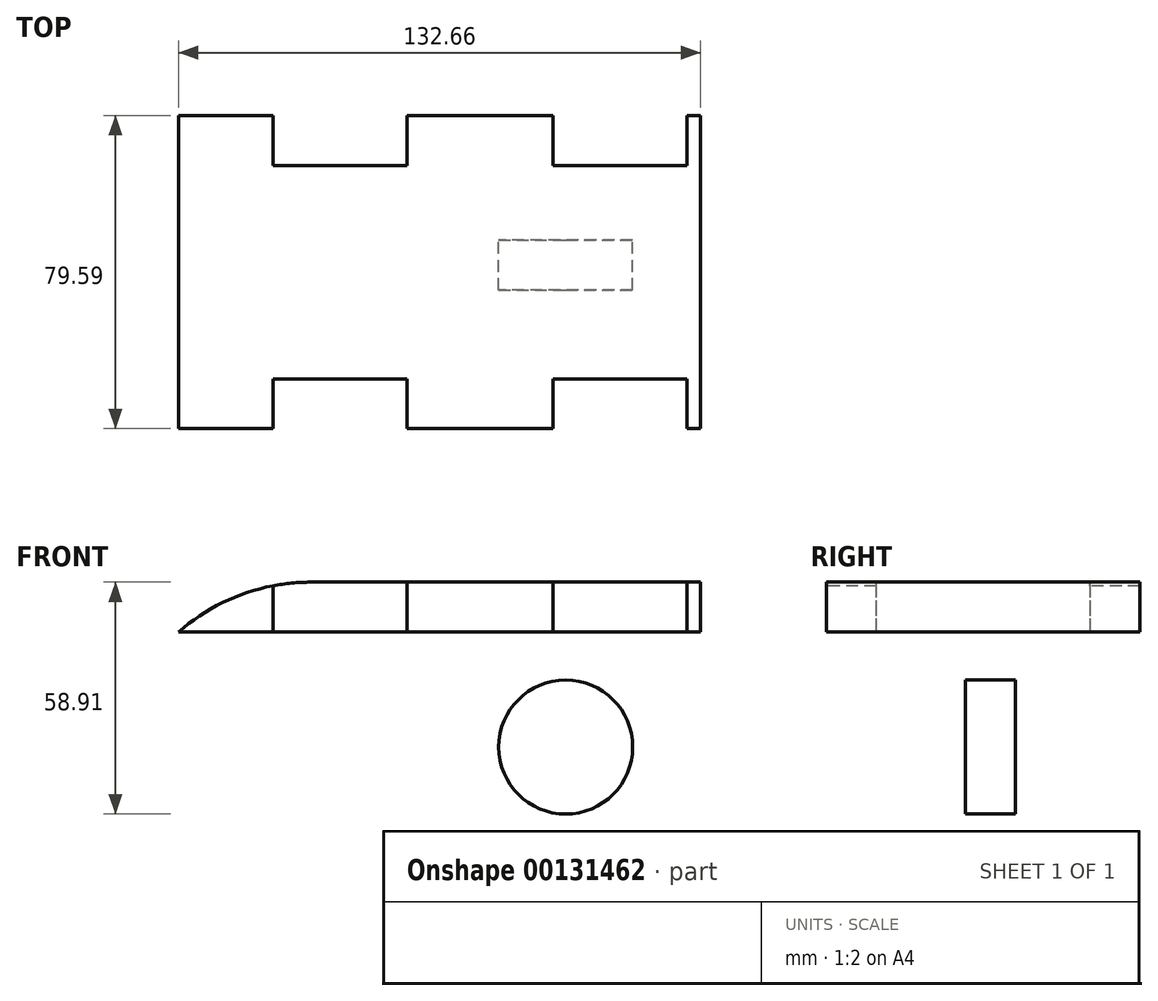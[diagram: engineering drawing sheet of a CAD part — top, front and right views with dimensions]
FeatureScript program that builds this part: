
annotation { "Feature Type Name" : "Feature", "Feature Type Description" : "" }
export const myFeature = defineFeature(function(context is Context, id is Id, definition is map)
    precondition{}
    {
        {
            var Q0;
            Q0=qCreatedBy(makeId("Top.planeOp"),FACE);
            var sketch = newSketch(context, id + "F0", { "sketchPlane" : qUnion([Q0])});
            skLineSegment(sketch, "E0.bottom", {"start": v(-58.03, 31.64) * mm, "end": v(74.63, 31.64) * mm});
            skLineSegment(sketch, "E0.top", {"start": v(-58.03, -47.95) * mm, "end": v(74.63, -47.95) * mm});
            skLineSegment(sketch, "E0.left", {"start": v(-58.03, 31.64) * mm, "end": v(-58.03, -47.95) * mm});
            skLineSegment(sketch, "E0.right", {"start": v(74.63, 31.64) * mm, "end": v(74.63, -47.95) * mm});
            skLineSegment(sketch, "E1.bottom", {"start": v(-34.04, 31.64) * mm, "end": v(0, 31.64) * mm});
            skLineSegment(sketch, "E1.top", {"start": v(-34.04, 18.94) * mm, "end": v(0, 18.94) * mm});
            skLineSegment(sketch, "E1.left", {"start": v(-34.04, 31.64) * mm, "end": v(-34.04, 18.94) * mm});
            skLineSegment(sketch, "E1.right", {"start": v(0, 31.64) * mm, "end": v(0, 18.94) * mm});
            skLineSegment(sketch, "E2.bottom", {"start": v(37.18, 31.64) * mm, "end": v(71.22, 31.64) * mm});
            skLineSegment(sketch, "E2.top", {"start": v(37.18, 18.94) * mm, "end": v(71.22, 18.94) * mm});
            skLineSegment(sketch, "E2.left", {"start": v(37.18, 31.64) * mm, "end": v(37.18, 18.94) * mm});
            skLineSegment(sketch, "E2.right", {"start": v(71.22, 31.64) * mm, "end": v(71.22, 18.94) * mm});
            skLineSegment(sketch, "E3.top", {"start": v(-34.04, -47.95) * mm, "end": v(0, -47.95) * mm});
            skLineSegment(sketch, "E3.left", {"start": v(-34.04, -35.34) * mm, "end": v(-34.04, -47.95) * mm});
            skLineSegment(sketch, "E3.right", {"start": v(0, -35.34) * mm, "end": v(0, -47.95) * mm});
            skLineSegment(sketch, "E4.top", {"start": v(37.18, -47.95) * mm, "end": v(71.22, -47.95) * mm});
            skLineSegment(sketch, "E4.left", {"start": v(37.18, -35.34) * mm, "end": v(37.18, -47.95) * mm});
            skLineSegment(sketch, "E4.right", {"start": v(71.22, -35.34) * mm, "end": v(71.22, -47.95) * mm});
            skLineSegment(sketch, "E5", {"start": v(37.18, -35.34) * mm, "end": v(71.22, -35.34) * mm});
            skLineSegment(sketch, "E6", {"start": v(0, -35.34) * mm, "end": v(-34.04, -35.34) * mm});
            skPoint(sketch, "E4.bottom.start.orphan", {"position": v(37.18, 14.58) * mm});
            skPoint(sketch, "E7.orphan", {"position": v(-34.04, 15) * mm});
            skSolve(sketch);
        }
        {
            var Q0;
            Q0=makeQuery(id+"F0.imprint","IMPRINT",FACE,{"disambiguationData":[TD([[makeQuery(id+"F0.imprint","IMPRINT",EDGE,{"derivedFrom":sQuery(id+"F0.wireOp",EDGE,"E0.bottom")}),-1.0]])]});
            extrude(context, id + "F1", {"entities" : qUnion([Q0]), "depth" : 12.7 * mm});
        }
        {
            var Q0;
            Q0=makeQuery(id+"F1.opExtrude","CAP_EDGE",EDGE,{"disambiguationData":[OSD([sQuery(id+"F0.wireOp",EDGE,"E0.left")])],"isStart":false});
            fillet(context, id + "F2", {"entities" : qUnion([Q0]), "radius" : 50.8 * mm, "tangentPropagation" : true, "allowEdgeOverflow" : false});
        }
        {
            var Q0;
            Q0=qCreatedBy(makeId("Front.planeOp"),FACE);
            var sketch = newSketch(context, id + "F3", { "sketchPlane" : qUnion([Q0])});
            skCircle(sketch, "E8", {"center": v(40.37, -29.19) * mm, "radius": 17.02 * mm});
            skSolve(sketch);
        }
        {
            var Q0;
            Q0=makeQuery(id+"F3.imprint","IMPRINT",FACE,{"disambiguationData":[TD([[makeQuery(id+"F3.imprint","IMPRINT",EDGE,{"derivedFrom":sQuery(id+"F3.wireOp",EDGE,"E8")}),1.0]])]});
            extrude(context, id + "F4", {"entities" : qUnion([Q0]), "depth" : 12.7 * mm});
        }
    });
